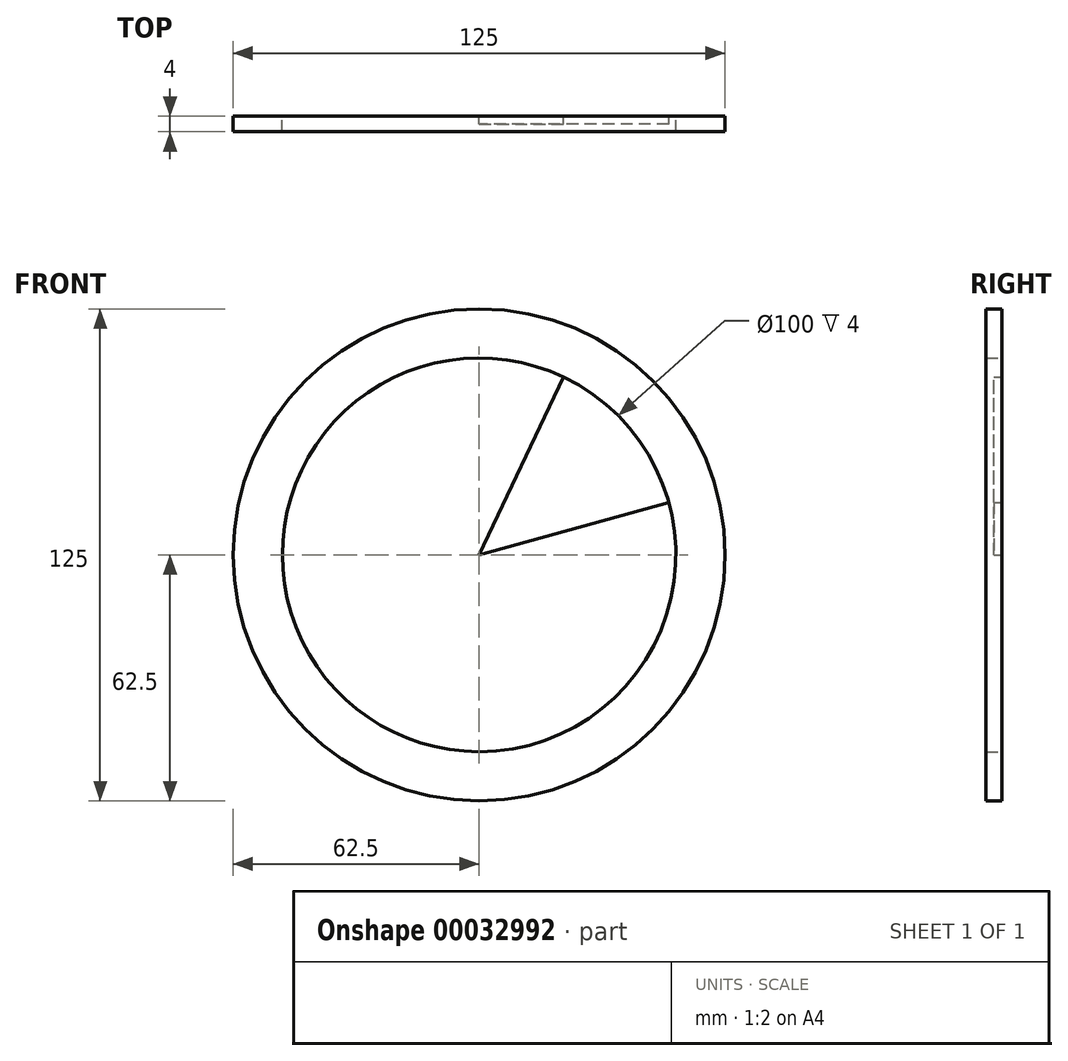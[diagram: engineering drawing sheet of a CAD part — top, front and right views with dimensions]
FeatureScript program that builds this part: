
annotation { "Feature Type Name" : "Feature", "Feature Type Description" : "" }
export const myFeature = defineFeature(function(context is Context, id is Id, definition is map)
    precondition{}
    {
        {
            var Q0;
            Q0=qCreatedBy(makeId("Front.planeOp"),FACE);
            var sketch = newSketch(context, id + "F0", { "sketchPlane" : qUnion([Q0])});
            skCircle(sketch, "E0", {"center": v(0, 0) * mm, "radius": 50 * mm});
            skCircle(sketch, "E1", {"center": v(0, 0) * mm, "radius": 62.5 * mm});
            skSolve(sketch);
        }
        {
            var Q0;
            Q0=makeQuery(id+"F0.imprint","IMPRINT",FACE,{"disambiguationData":[TD([[makeQuery(id+"F0.imprint","IMPRINT",EDGE,{"derivedFrom":sQuery(id+"F0.wireOp",EDGE,"E0")}),-1.0]])]});
            extrude(context, id + "F1", {"entities" : qUnion([Q0]), "depth" : 4 * mm});
        }
        {
            var Q0;
            Q0=qCreatedBy(makeId("Front.planeOp"),FACE);
            var sketch = newSketch(context, id + "F2", { "sketchPlane" : qUnion([Q0])});
            skCircle(sketch, "E2", {"center": v(0, 0) * mm, "radius": 56.32 * mm});
            skLineSegment(sketch, "E3", {"start": v(54.28, 15.02) * mm, "end": v(0, 0) * mm});
            skLineSegment(sketch, "E4", {"start": v(0, 0) * mm, "end": v(24.19, 50.86) * mm});
            skLineSegment(sketch, "E5", {"start": v(24.19, 50.86) * mm, "end": v(54.28, 15.02) * mm});
            skSolve(sketch);
        }
        {
            var Q0;
            Q0=makeQuery(id+"F2.imprint","IMPRINT",FACE,{"disambiguationData":[TD([[makeQuery(id+"F2.imprint","IMPRINT",EDGE,{"derivedFrom":sQuery(id+"F2.wireOp",EDGE,"E3")}),-1.0]])]});
            extrude(context, id + "F3", {"entities" : qUnion([Q0]), "operationType" : NewBodyOperationType.ADD, "depth" : 2 * mm});
        }
    });
